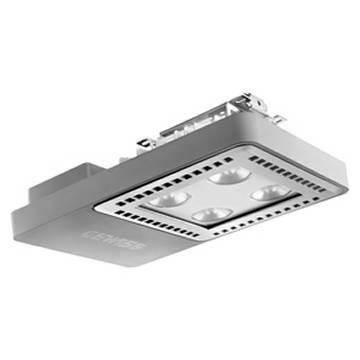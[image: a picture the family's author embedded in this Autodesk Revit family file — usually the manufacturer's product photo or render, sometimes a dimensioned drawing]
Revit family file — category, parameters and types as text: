
# Revit family: Lighting-Industriale-GEWISS-SMART[4]HT_APPARECCHI-LED_1M
name_source: partatom
category: Apparecchi per illuminazione
units: mm (PartAtom-declared; Revit-internal decimal feet)

## family parameters
Basato su piano di lavoro = Sì
Condiviso = No
Numero OmniClass = 23.80.00.00
Punto di calcolo locali = No
Quota connettore circolare = Usa diametro
Sempre verticale = No
Sorgente d'illuminazione = No
Taglio con vuoti quando caricato = No
Tipo di parte = Normale
Titolo OmniClass = Electric Power and Lighting

## types (1)
- Lighting-Industriale-GEWISS-SMART[4]HT_APPARECCHI-LED_1M
    Alimentatore = Incluso
    Apparecchio a ridotta temperatura superficiale = Si
    Applicazione = Interno
    Cablaggio = Con connettore stagno Gw connect
    Caratteristiche elettriche e gestione della luce = -
    Caratteristiche ottiche e illuminotecniche = -
    Carico apparente = 50 VA
    Catalogo = LIGHTING
    Certificazione DIN 18032-3 = -
    Certificazioni e classificazioni = -
    Classe fotobiologica = RG0
    Classe isolamento = I
    Classificazione = Lighting
    Classificazione: = -
    Codice Electrocod = 2444
    Codice digitale univoco (Datamatrix) = Datamatrix
    Colore = Grigio RAL 7035
    Commenti sul wattaggio = 50W
    Contesto = Illuminazione di logistiche e locali produttivi industriali
    Controllo abbagliamento e luminanza = -
    Corpo = PA6 “Halogen Free” caricato fibra vetro
    Descrizione = SMART[4]LB 1M ST.AL.ON/OFF HT ELL.57K
    Dispositivo di protezione = DM 6 kV / CM 10 kV
    Distanza tot_plafoniera = 74 mm  [stored 0.242782 ft]
    Durata di vita = L90B10 (Tq+25°C) = 100.000 h - L90B10 (Tq+60°C) = 50.000 h
    Efficienza luminosa (lm/W) = 131
    Finitura colore = Grigio RAL 7035
    Fissaggio = -
    Frequenza nominale (Hz) = 50/60 Hz
    Gancio di chiusura = -
    Garanzia = 5 anni
    Grado di protezione = IP66
    Gruppo ottico = Riflettore in PC metallizzato e lenti in PMMA
    Guarnizioni = tipo siliconico antinvecchiamento
    IDF = 7e642e0c-a44c-4e04-8a4c-7356ce50b369
    IDT = 36f92d81beab46f4b5fefa69774160e7
    IPEA = -
    Immagine tipo = GWL1071.jpg
    Inclinazione = Con accessorio staffa
    Indice di resa cromatica = CRI-80
    Informazioni generali = -
    Installazione e manutenzione = -
    Lampada = LED
    Larghezza = 253 mm  [stored 0.830052 ft]
    Lumen output (lm) = 6300
    Lunghezza = 383 mm  [stored 1.25656 ft]
    Materiali = -
    Modello = GWS4120CQ857
    Motore = <Per categoria>
    Norma di riferimento = EN 60598-1 ; EN 60598-2-1 ; EN 60598-2-24
    Ottica = Ellittica
    Peso (kg): = 3,5
    Plafoniera = <Per categoria>
    Potenza di sistema = 48W
    Produttore = GEWISS S.p.A.
    Prospetto di default = 1219 mm
    Raggio led = 30 mm  [stored 0.0984252 ft]
    Resistenza agli urti = IK08
    Resistenza al filo incandescente = 850 °C
    SEO = Low Bay
    Scheda Tecnica = https://www.gewiss.com
    Schermo = Vetro Temprato Spessore 4mm
    Sistema di controllo = ON / OFF
    Sistema di controllo : = ON / OFF
    Sostituibilità gruppo ottico = Non sostituibile
    Sostituibilità piastra di cablaggio = Non sostituibile
    Spessore plafoniera = 40 mm
    Superficie massima esposta al vento : = 0,097 m²
    Temperatura di colore = 5700K
    Temperatura di esercizio = -30°C ÷ +60 °C
    Temperatura di stoccaggio = -40 +70 °C
    Tensione di alimentazione = 220 - 240 V
    Tipo di apparecchio = Riflettore industriale a LED&nbsp;
    Tipo di installazione e montaggio = Plafone - Parete - Sospensione
    Tipologia sorgente luminosa = LED - Non sostituibile
    Tolleranza cromatica = SDCM = 3
    Trasformatore = <Per categoria>
    URL = https://www.gewiss.com
    Vano di alimentazione = Integrato
    Versione file RFA = 20.11
    Vetro acceso = Lampada accesa
    Viti esterne = Acciaio inox
    Voltaggio = 230 V

note: [stored X ft] marks values corroborated as IEEE doubles in the binary element streams (Revit-internal decimal feet)

## geometry (parser evidence)
native form markers: Blend x4
no freeform markers — native parametric forms only
